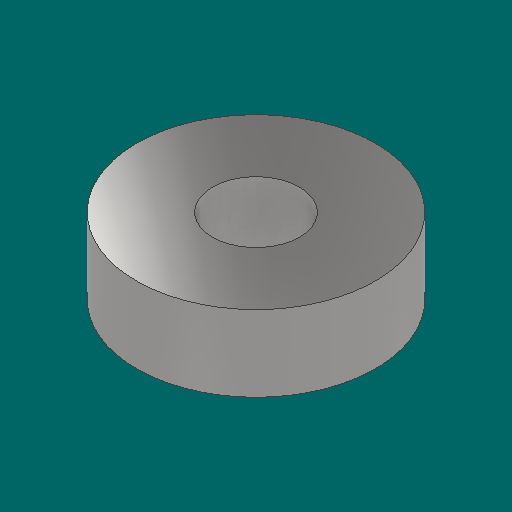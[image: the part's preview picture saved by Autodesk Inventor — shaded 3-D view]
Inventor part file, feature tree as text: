
AUTODESK INVENTOR PART (.ipt)
format: ipt  version: 2023.1 (Build 271208000, 208)  size: 107,520 bytes
history: native  units: in
note: dims shown in document units (in); Inventor stores cm internally (conversion verified against a paired STEP export)
features: other x3, sketch x1
ambient origin geometry x8: Origin, YZ Plane, XZ Plane, XY Plane, X Axis, Y Axis, Z Axis, Center Point
bodies: Solid1 (feature_tree)
feature tree (4):
  other  "608bearing_MIR.ipt"
  other  "Solid1::608bearing_MIR.ipt"
  other  "TaggingFeature1"
  sketch  "Sketch1"  dims[d0=0.3937in]
